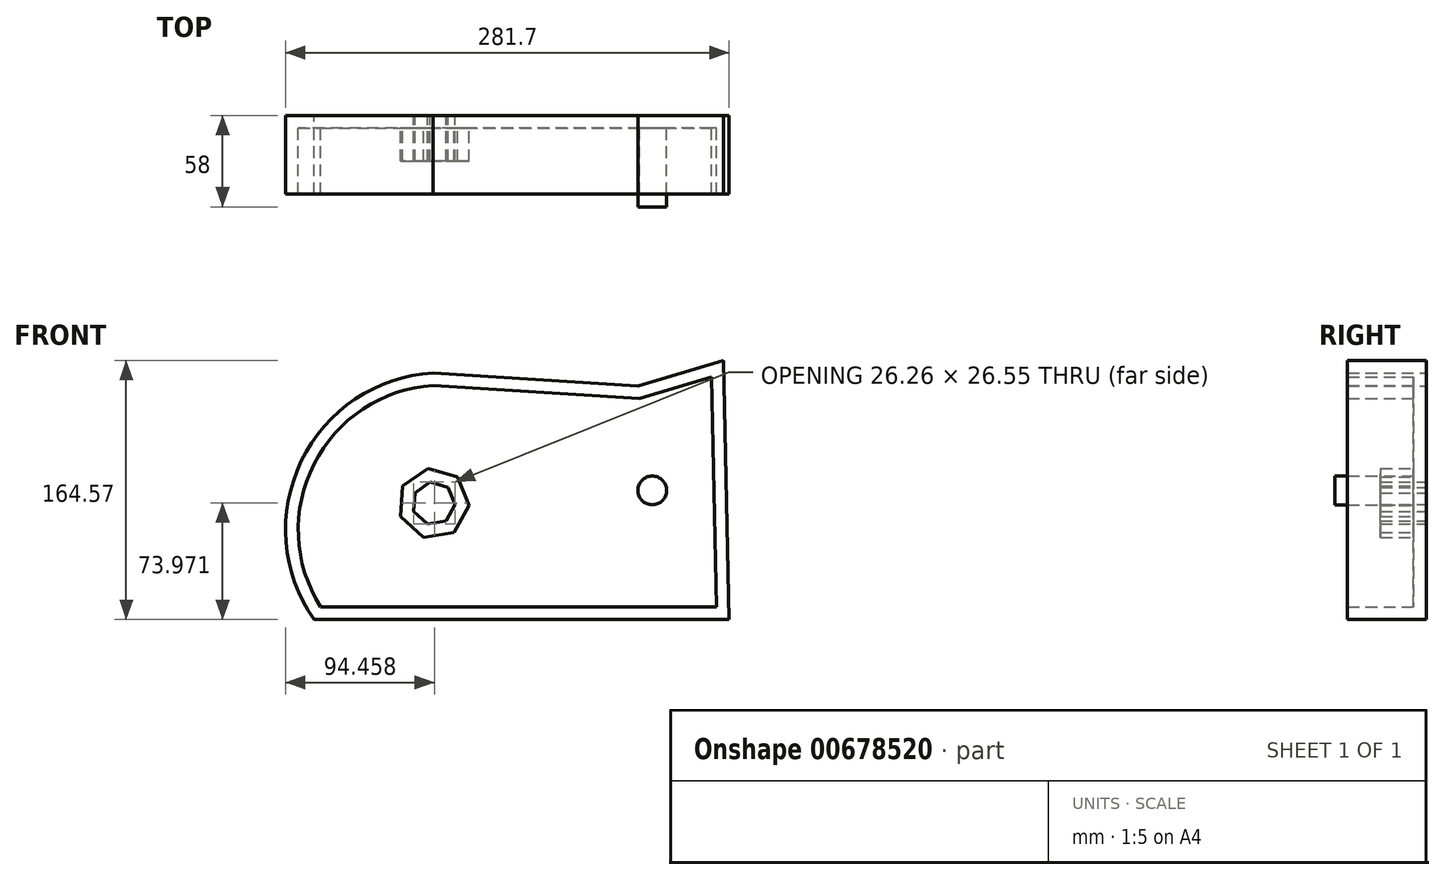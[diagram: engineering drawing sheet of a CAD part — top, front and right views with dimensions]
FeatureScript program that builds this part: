
annotation { "Feature Type Name" : "Feature", "Feature Type Description" : "" }
export const myFeature = defineFeature(function(context is Context, id is Id, definition is map)
    precondition{}
    {
        {
            var Q0;
            Q0=qCreatedBy(makeId("Front.planeOp"),FACE);
            var sketch = newSketch(context, id + "F0", { "sketchPlane" : qUnion([Q0])});
            skCircle(sketch, "E0", {"center": v(0, 0) * mm, "radius": 53.72 * mm});
            skCircle(sketch, "E1", {"center": v(0, 0) * mm, "radius": 58.67 * mm, "construction": true});
            skCircle(sketch, "E2", {"center": v(0, 0) * mm, "radius": 63.5 * mm, "construction": true});
            skLineSegment(sketch, "E3", {"start": v(0, 0) * mm, "end": v(0, 100.95) * mm, "construction": true});
            skLineSegment(sketch, "E4", {"start": v(0, 0) * mm, "end": v(-5.95, 90.82) * mm, "construction": true});
            skLineSegment(sketch, "E5", {"start": v(0, 58.67) * mm, "end": v(-49.43, 58.67) * mm, "construction": true});
            skLineSegment(sketch, "E6", {"start": v(0, 58.67) * mm, "end": v(-58.4, 37.42) * mm, "construction": true});
            skCircle(sketch, "E7", {"center": v(0, 0) * mm, "radius": 55.14 * mm, "construction": true});
            skCircle(sketch, "E8", {"center": v(0, 58.67) * mm, "radius": 14.6 * mm, "construction": true});
            skCircle(sketch, "E9", {"center": v(-13.72, 53.68) * mm, "radius": 14.6 * mm, "construction": true});
            skArc(sketch, "E10", {"start": v(0, 58.67) * mm, "mid": v(-1.2, 61.19) * mm, "end": v(-2.86, 63.44) * mm});
            skArc(sketch, "E11", {"start": v(0.88, 53.71) * mm, "mid": v(0.67, 56.23) * mm, "end": v(0, 58.67) * mm});
            skArc(sketch, "E12.MirrorCS", {"start": v(-7.66, 58.17) * mm, "mid": v(-6.79, 60.82) * mm, "end": v(-5.45, 63.27) * mm});
            skArc(sketch, "E13.MirrorCS", {"start": v(-7.88, 53.14) * mm, "mid": v(-8, 55.67) * mm, "end": v(-7.66, 58.17) * mm});
            skArc(sketch, "E14", {"start": v(-2.86, 63.44) * mm, "mid": v(-4.17, 63.6) * mm, "end": v(-5.45, 63.27) * mm});
            skCircle(sketch, "E15.cCircle", {"center": v(0, 0) * mm, "radius": 30.67 * mm, "construction": true});
            skLineSegment(sketch, "E15.0", {"start": v(-20.6, -28.8) * mm, "end": v(-35.25, 3.45) * mm});
            skLineSegment(sketch, "E15.1", {"start": v(-35.25, 3.45) * mm, "end": v(-14.64, 32.25) * mm});
            skLineSegment(sketch, "E15.2", {"start": v(-14.64, 32.25) * mm, "end": v(20.6, 28.8) * mm});
            skLineSegment(sketch, "E15.3", {"start": v(20.6, 28.8) * mm, "end": v(35.25, -3.45) * mm});
            skLineSegment(sketch, "E15.4", {"start": v(35.25, -3.45) * mm, "end": v(14.64, -32.25) * mm});
            skLineSegment(sketch, "E15.5", {"start": v(14.64, -32.25) * mm, "end": v(-20.6, -28.8) * mm});
            skPoint(sketch, "E15.0.midPoint", {"position": v(-27.93, -12.68) * mm});
            skCircle(sketch, "E16.cCircle", {"center": v(0, 0) * mm, "radius": 12.3 * mm, "construction": true});
            skLineSegment(sketch, "E16.0", {"start": v(-3.88, -13.08) * mm, "end": v(-12.64, -5.13) * mm});
            skLineSegment(sketch, "E16.1", {"start": v(-12.64, -5.13) * mm, "end": v(-11.9, 6.69) * mm});
            skLineSegment(sketch, "E16.2", {"start": v(-11.9, 6.69) * mm, "end": v(-2.19, 13.47) * mm});
            skLineSegment(sketch, "E16.3", {"start": v(-2.19, 13.47) * mm, "end": v(9.17, 10.1) * mm});
            skLineSegment(sketch, "E16.4", {"start": v(9.17, 10.1) * mm, "end": v(13.62, -0.87) * mm});
            skLineSegment(sketch, "E16.5", {"start": v(13.62, -0.87) * mm, "end": v(7.81, -11.19) * mm});
            skLineSegment(sketch, "E16.6", {"start": v(7.81, -11.19) * mm, "end": v(-3.88, -13.08) * mm});
            skPoint(sketch, "E16.0.midPoint", {"position": v(-8.26, -9.1) * mm});
            skSolve(sketch);
        }
        {
            var Q0;
            {var subQ0=sQuery(id+"F0.wireOp",EDGE,"E0");var subQ1=makeQuery(id+"F0.imprint","INTERSECT",VERTEX,{"derivedFrom":[subQ0,sQuery(id+"F0.wireOp",EDGE,"E11")]});Q0=makeQuery(id+"F0.imprint","IMPRINT",FACE,{"disambiguationData":[TD([[makeQuery(id+"F0.imprint","IMPRINT",EDGE,{"disambiguationData":[TD([[subQ1,-1.0]])],"derivedFrom":subQ0}),1.0]])]});}
            var Q1;
            Q1=makeQuery(id+"F0.imprint","IMPRINT",FACE,{"disambiguationData":[TD([[makeQuery(id+"F0.imprint","IMPRINT",EDGE,{"derivedFrom":sQuery(id+"F0.wireOp",EDGE,"E10")}),1.0]])]});
            extrude(context, id + "F1", {"entities" : qUnion([Q0, Q1]), "depth" : 25 * mm, "offsetDistance" : 25 * mm});
        }
        {
            var Q0;
            Q0=makeQuery(id+"F1.opExtrude","SWEPT_BODY",BODY,{"disambiguationData":[OSD([sQuery(id+"F0.wireOp",EDGE,"E0"),sQuery(id+"F0.wireOp",EDGE,"E10"),sQuery(id+"F0.wireOp",EDGE,"E11"),sQuery(id+"F0.wireOp",EDGE,"E12.MirrorCS"),sQuery(id+"F0.wireOp",EDGE,"E13.MirrorCS"),sQuery(id+"F0.wireOp",EDGE,"E14")])]});
            var Q1;
            Q1=makeQuery(id+"F1.opExtrude","SWEPT_FACE",FACE,{"disambiguationData":[OSD([sQuery(id+"F0.wireOp",EDGE,"E0")])]});
            circularPattern(context, id + "F2", {"entities" : qUnion([Q0]), "axis" : qUnion([Q1]), "angle" : 360 * degree, "instanceCount" : 24, "equalSpace" : true});
        }
        {
            var Q0;
            Q0=makeQuery(id+"F0.imprint","IMPRINT",FACE,{"disambiguationData":[TD([[makeQuery(id+"F0.imprint","IMPRINT",EDGE,{"derivedFrom":sQuery(id+"F0.wireOp",EDGE,"E15.0")}),-1.0]])]});
            extrude(context, id + "F3", {"entities" : qUnion([Q0]), "operationType" : NewBodyOperationType.ADD, "depth" : 40 * mm, "offsetDistance" : 25 * mm});
        }
        {
            var Q0;
            {var subQ0=makeQuery(id+"F1.opExtrude","CAP_FACE",FACE,{"disambiguationData":[OSD([sQuery(id+"F0.wireOp",EDGE,"E0"),sQuery(id+"F0.wireOp",EDGE,"E10"),sQuery(id+"F0.wireOp",EDGE,"E11"),sQuery(id+"F0.wireOp",EDGE,"E12.MirrorCS"),sQuery(id+"F0.wireOp",EDGE,"E13.MirrorCS"),sQuery(id+"F0.wireOp",EDGE,"E14"),sQuery(id+"F0.wireOp",EDGE,"E15.0"),sQuery(id+"F0.wireOp",EDGE,"E15.1"),sQuery(id+"F0.wireOp",EDGE,"E15.2"),sQuery(id+"F0.wireOp",EDGE,"E15.3"),sQuery(id+"F0.wireOp",EDGE,"E15.4"),sQuery(id+"F0.wireOp",EDGE,"E15.5")])],"isStart":false});Q0=makeQuery(id+"F3.boolean.opBoolean","MERGE",FACE,{"derivedFrom":[subQ0,makeQuery(id+"F2.opPattern","COPY",FACE,{"derivedFrom":subQ0,"instanceName":"1"}),makeQuery(id+"F2.opPattern","COPY",FACE,{"derivedFrom":subQ0,"instanceName":"2"}),makeQuery(id+"F2.opPattern","COPY",FACE,{"derivedFrom":subQ0,"instanceName":"3"}),makeQuery(id+"F2.opPattern","COPY",FACE,{"derivedFrom":subQ0,"instanceName":"4"}),makeQuery(id+"F2.opPattern","COPY",FACE,{"derivedFrom":subQ0,"instanceName":"5"}),makeQuery(id+"F2.opPattern","COPY",FACE,{"derivedFrom":subQ0,"instanceName":"6"}),makeQuery(id+"F2.opPattern","COPY",FACE,{"derivedFrom":subQ0,"instanceName":"7"}),makeQuery(id+"F2.opPattern","COPY",FACE,{"derivedFrom":subQ0,"instanceName":"8"}),makeQuery(id+"F2.opPattern","COPY",FACE,{"derivedFrom":subQ0,"instanceName":"9"}),makeQuery(id+"F2.opPattern","COPY",FACE,{"derivedFrom":subQ0,"instanceName":"10"}),makeQuery(id+"F2.opPattern","COPY",FACE,{"derivedFrom":subQ0,"instanceName":"11"}),makeQuery(id+"F2.opPattern","COPY",FACE,{"derivedFrom":subQ0,"instanceName":"12"}),makeQuery(id+"F2.opPattern","COPY",FACE,{"derivedFrom":subQ0,"instanceName":"13"}),makeQuery(id+"F2.opPattern","COPY",FACE,{"derivedFrom":subQ0,"instanceName":"14"}),makeQuery(id+"F2.opPattern","COPY",FACE,{"derivedFrom":subQ0,"instanceName":"15"}),makeQuery(id+"F2.opPattern","COPY",FACE,{"derivedFrom":subQ0,"instanceName":"16"}),makeQuery(id+"F2.opPattern","COPY",FACE,{"derivedFrom":subQ0,"instanceName":"17"}),makeQuery(id+"F2.opPattern","COPY",FACE,{"derivedFrom":subQ0,"instanceName":"18"}),makeQuery(id+"F2.opPattern","COPY",FACE,{"derivedFrom":subQ0,"instanceName":"19"}),makeQuery(id+"F2.opPattern","COPY",FACE,{"derivedFrom":subQ0,"instanceName":"20"}),makeQuery(id+"F2.opPattern","COPY",FACE,{"derivedFrom":subQ0,"instanceName":"21"}),makeQuery(id+"F2.opPattern","COPY",FACE,{"derivedFrom":subQ0,"instanceName":"22"}),makeQuery(id+"F2.opPattern","COPY",FACE,{"derivedFrom":subQ0,"instanceName":"23"})]});}
            var Q1;
            Q1=makeQuery(id+"F3.opExtrude","CAP_FACE",FACE,{"disambiguationData":[OSD([sQuery(id+"F0.wireOp",EDGE,"E15.0"),sQuery(id+"F0.wireOp",EDGE,"E15.1"),sQuery(id+"F0.wireOp",EDGE,"E15.2"),sQuery(id+"F0.wireOp",EDGE,"E15.3"),sQuery(id+"F0.wireOp",EDGE,"E15.4"),sQuery(id+"F0.wireOp",EDGE,"E15.5"),sQuery(id+"F0.wireOp",EDGE,"E16.0"),sQuery(id+"F0.wireOp",EDGE,"E16.1"),sQuery(id+"F0.wireOp",EDGE,"E16.2"),sQuery(id+"F0.wireOp",EDGE,"E16.3"),sQuery(id+"F0.wireOp",EDGE,"E16.4"),sQuery(id+"F0.wireOp",EDGE,"E16.5"),sQuery(id+"F0.wireOp",EDGE,"E16.6")])],"isStart":false});
            chamfer(context, id + "F4", {"entities" : qUnion([Q0, Q1]), "width" : 2 * mm, "tangentPropagation" : true});
        }
        {
            var Q0;
            Q0=qCreatedBy(makeId("Front.planeOp"),FACE);
            var sketch = newSketch(context, id + "F5", { "sketchPlane" : qUnion([Q0])});
            skArc(sketch, "E17", {"start": v(0, 82.68) * mm, "mid": v(-83.7, 26.52) * mm, "end": v(-75.68, -73.97) * mm});
            skLineSegment(sketch, "E18.0", {"start": v(-3.54, -13.27) * mm, "end": v(-12.31, -5.32) * mm});
            skLineSegment(sketch, "E18.1", {"start": v(-12.31, -5.32) * mm, "end": v(-11.56, 6.5) * mm});
            skLineSegment(sketch, "E18.2", {"start": v(-11.56, 6.5) * mm, "end": v(-1.85, 13.28) * mm});
            skLineSegment(sketch, "E18.3", {"start": v(-1.85, 13.28) * mm, "end": v(9.5, 9.91) * mm});
            skLineSegment(sketch, "E18.4", {"start": v(9.5, 9.91) * mm, "end": v(13.95, -1.06) * mm});
            skLineSegment(sketch, "E18.5", {"start": v(13.95, -1.06) * mm, "end": v(8.14, -11.38) * mm});
            skLineSegment(sketch, "E18.6", {"start": v(8.14, -11.38) * mm, "end": v(-3.54, -13.27) * mm});
            skLineSegment(sketch, "E19", {"start": v(-75.68, -73.97) * mm, "end": v(188.06, -73.97) * mm});
            skLineSegment(sketch, "E20", {"start": v(188.06, -73.97) * mm, "end": v(184.53, 90.6) * mm});
            skLineSegment(sketch, "E21", {"start": v(184.53, 90.6) * mm, "end": v(130.32, 74.41) * mm});
            skLineSegment(sketch, "E22", {"start": v(130.32, 74.41) * mm, "end": v(0, 82.68) * mm});
            skSolve(sketch);
        }
        {
            var Q0;
            Q0=makeQuery(id+"F5.imprint","IMPRINT",FACE,{"disambiguationData":[TD([[makeQuery(id+"F5.imprint","IMPRINT",EDGE,{"derivedFrom":sQuery(id+"F5.wireOp",EDGE,"E17")}),1.0]])]});
            extrude(context, id + "F6", {"entities" : qUnion([Q0]), "depth" : 50 * mm, "offsetDistance" : 25 * mm});
        }
        {
            var Q0;
            Q0=makeQuery(id+"F6.opExtrude","CAP_FACE",FACE,{"disambiguationData":[OSD([sQuery(id+"F5.wireOp",EDGE,"beejBg9F-YV6n-nufv-Nw4E-tFm8joiHm930"),sQuery(id+"F5.wireOp",EDGE,"8e5JYoWA-7fom-5Bzb-9iBh-hFW4UDGijwtQ"),sQuery(id+"F5.wireOp",EDGE,"lEZHPKjb-R6Zr-Jheq-EaUw-EQRS34ZE65Sm"),sQuery(id+"F5.wireOp",EDGE,"E17")])],"isStart":false});
            shell(context, id + "F7", {"entities" : qUnion([Q0]), "thickness" : 8 * mm});
        }
        {
            var Q0;
            Q0=makeQuery(id+"F6.opExtrude","CAP_FACE",FACE,{"disambiguationData":[OSD([sQuery(id+"F5.wireOp",EDGE,"beejBg9F-YV6n-nufv-Nw4E-tFm8joiHm930"),sQuery(id+"F5.wireOp",EDGE,"8e5JYoWA-7fom-5Bzb-9iBh-hFW4UDGijwtQ"),sQuery(id+"F5.wireOp",EDGE,"lEZHPKjb-R6Zr-Jheq-EaUw-EQRS34ZE65Sm"),sQuery(id+"F5.wireOp",EDGE,"E17"),sQuery(id+"F5.wireOp",EDGE,"E18.0"),sQuery(id+"F5.wireOp",EDGE,"E18.1"),sQuery(id+"F5.wireOp",EDGE,"E18.2"),sQuery(id+"F5.wireOp",EDGE,"E18.3"),sQuery(id+"F5.wireOp",EDGE,"E18.4"),sQuery(id+"F5.wireOp",EDGE,"E18.5"),sQuery(id+"F5.wireOp",EDGE,"E18.6")])],"isStart":false});
            extrude(context, id + "F8", {"entities" : qUnion([Q0]), "operationType" : NewBodyOperationType.REMOVE, "oppositeDirection" : true, "depth" : 21 * mm, "offsetDistance" : 25 * mm});
        }
        {
            var Q0;
            {var subQ0=sQuery(id+"F5.wireOp",EDGE,"E18.6");var subQ1=sQuery(id+"F5.wireOp",EDGE,"E18.5");var subQ2=sQuery(id+"F5.wireOp",EDGE,"E18.4");var subQ3=sQuery(id+"F5.wireOp",EDGE,"E18.3");var subQ4=sQuery(id+"F5.wireOp",EDGE,"E18.2");var subQ5=sQuery(id+"F5.wireOp",EDGE,"E18.1");var subQ6=sQuery(id+"F5.wireOp",EDGE,"E18.0");var subQ7=sQuery(id+"F5.wireOp",EDGE,"E17");var subQ8=sQuery(id+"F5.wireOp",EDGE,"lEZHPKjb-R6Zr-Jheq-EaUw-EQRS34ZE65Sm");var subQ9=sQuery(id+"F5.wireOp",EDGE,"8e5JYoWA-7fom-5Bzb-9iBh-hFW4UDGijwtQ");var subQ10=sQuery(id+"F5.wireOp",EDGE,"beejBg9F-YV6n-nufv-Nw4E-tFm8joiHm930");Q0=makeQuery(id+"F7.opShell","OFFSET_FACE",FACE,{"disambiguationData":[OSD([subQ10,subQ9,subQ8,subQ7,subQ6,subQ5,subQ4,subQ3,subQ2,subQ1,subQ0]),TDD([makeQuery(id+"F6.opExtrude","CAP_FACE",FACE,{"disambiguationData":[OSD([subQ10,subQ9,subQ8,subQ7,subQ6,subQ5,subQ4,subQ3,subQ2,subQ1,subQ0])],"isStart":true})])]});}
            var sketch = newSketch(context, id + "F9", { "sketchPlane" : qUnion([Q0])});
            skCircle(sketch, "E23", {"center": v(139.25, 7.97) * mm, "radius": 9.13 * mm});
            skSolve(sketch);
        }
        {
            var Q0;
            Q0=makeQuery(id+"F9.imprint","IMPRINT",FACE,{"disambiguationData":[TD([[makeQuery(id+"F9.imprint","IMPRINT",EDGE,{"derivedFrom":sQuery(id+"F9.wireOp",EDGE,"E23")}),1.0]])]});
            extrude(context, id + "F10", {"entities" : qUnion([Q0]), "operationType" : NewBodyOperationType.ADD, "depth" : 50 * mm, "offsetDistance" : 25 * mm});
        }
        {
            var Q0;
            Q0=makeQuery(id+"F1.opExtrude","SWEPT_BODY",BODY,{"disambiguationData":[OSD([sQuery(id+"F0.wireOp",EDGE,"E0"),sQuery(id+"F0.wireOp",EDGE,"E10"),sQuery(id+"F0.wireOp",EDGE,"E11"),sQuery(id+"F0.wireOp",EDGE,"E12.MirrorCS"),sQuery(id+"F0.wireOp",EDGE,"E13.MirrorCS"),sQuery(id+"F0.wireOp",EDGE,"E14"),sQuery(id+"F0.wireOp",EDGE,"E15.0"),sQuery(id+"F0.wireOp",EDGE,"E15.1"),sQuery(id+"F0.wireOp",EDGE,"E15.2"),sQuery(id+"F0.wireOp",EDGE,"E15.3"),sQuery(id+"F0.wireOp",EDGE,"E15.4"),sQuery(id+"F0.wireOp",EDGE,"E15.5")])]});
            deleteBodies(context, id + "F11", {"entities" : qUnion([Q0])});
        }
    });
